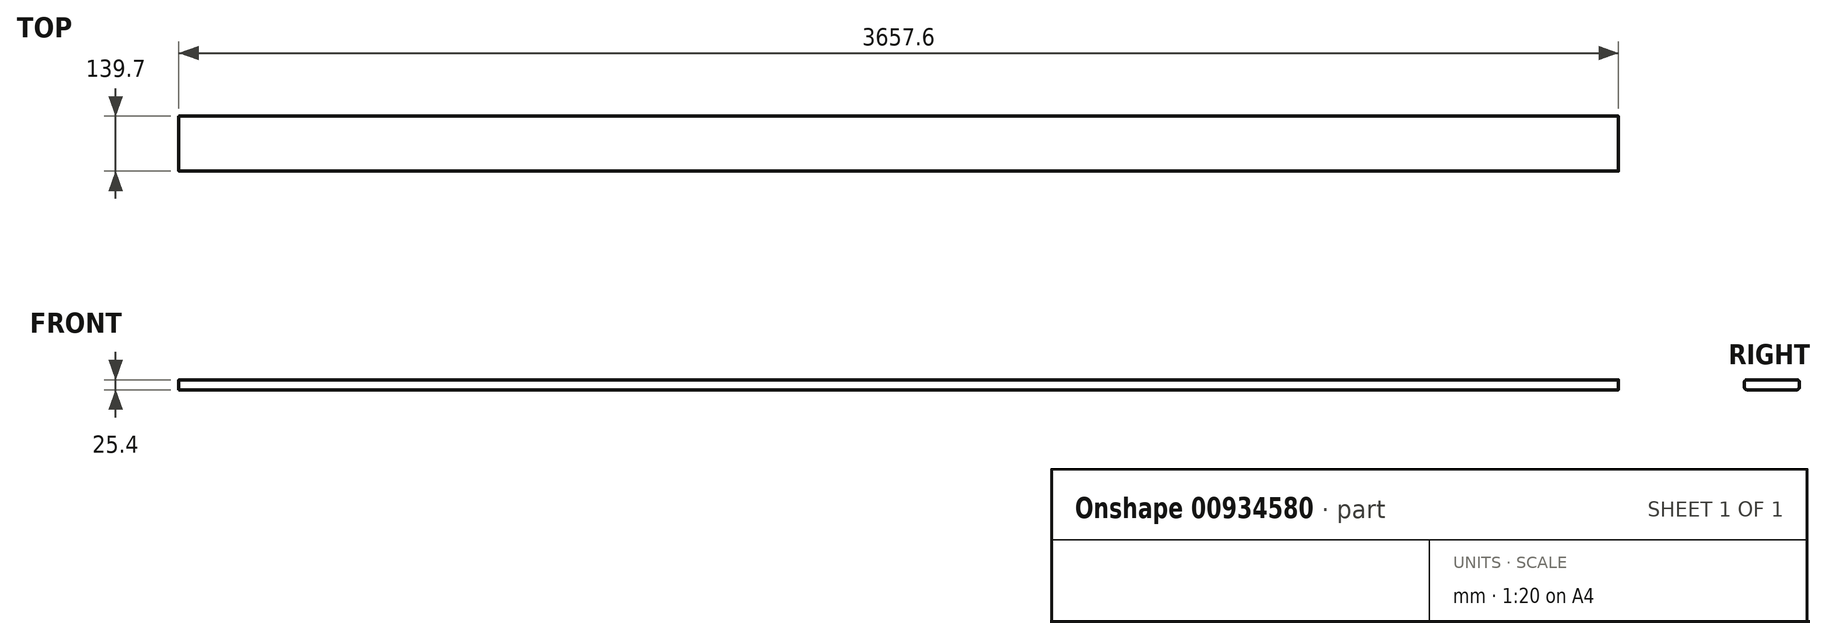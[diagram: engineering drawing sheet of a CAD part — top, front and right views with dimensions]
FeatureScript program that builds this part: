
annotation { "Feature Type Name" : "Feature", "Feature Type Description" : "" }
export const myFeature = defineFeature(function(context is Context, id is Id, definition is map)
    precondition{}
    {
        {
            var Q0;
            Q0=qCreatedBy(makeId("Right.planeOp"),FACE);
            var sketch = newSketch(context, id + "F0", { "sketchPlane" : qUnion([Q0])});
            skLineSegment(sketch, "E0.bottom", {"start": v(188.06, 206.2) * mm, "end": v(315.06, 206.2) * mm});
            skLineSegment(sketch, "E0.top", {"start": v(188.06, 180.8) * mm, "end": v(315.06, 180.8) * mm});
            skLineSegment(sketch, "E0.left", {"start": v(181.71, 199.86) * mm, "end": v(181.71, 187.16) * mm});
            skLineSegment(sketch, "E0.right", {"start": v(321.41, 199.86) * mm, "end": v(321.41, 187.16) * mm});
            skPoint(sketch, "E1.visualSharp", {"position": v(321.41, 206.2) * mm});
            skArc(sketch, "E1.filletArc", {"start": v(321.41, 199.86) * mm, "mid": v(319.55, 204.35) * mm, "end": v(315.06, 206.2) * mm});
            skPoint(sketch, "E2.visualSharp", {"position": v(321.41, 180.8) * mm});
            skArc(sketch, "E2.filletArc", {"start": v(315.06, 180.8) * mm, "mid": v(319.55, 182.67) * mm, "end": v(321.41, 187.16) * mm});
            skPoint(sketch, "E3.visualSharp", {"position": v(181.71, 206.2) * mm});
            skArc(sketch, "E3.filletArc", {"start": v(188.06, 206.2) * mm, "mid": v(183.57, 204.35) * mm, "end": v(181.71, 199.86) * mm});
            skPoint(sketch, "E4.visualSharp", {"position": v(181.71, 180.8) * mm});
            skArc(sketch, "E4.filletArc", {"start": v(181.71, 187.16) * mm, "mid": v(183.57, 182.67) * mm, "end": v(188.06, 180.8) * mm});
            skSolve(sketch);
        }
        {
            var Q0;
            Q0=makeQuery(id+"F0.imprint","IMPRINT",FACE,{"disambiguationData":[TD([[makeQuery(id+"F0.imprint","IMPRINT",EDGE,{"derivedFrom":sQuery(id+"F0.wireOp",EDGE,"E0.bottom")}),-1.0]])]});
            extrude(context, id + "F1", {"entities" : qUnion([Q0]), "depth" : 3657.6 * mm, "offsetDistance" : 25.4 * mm});
        }
    });
